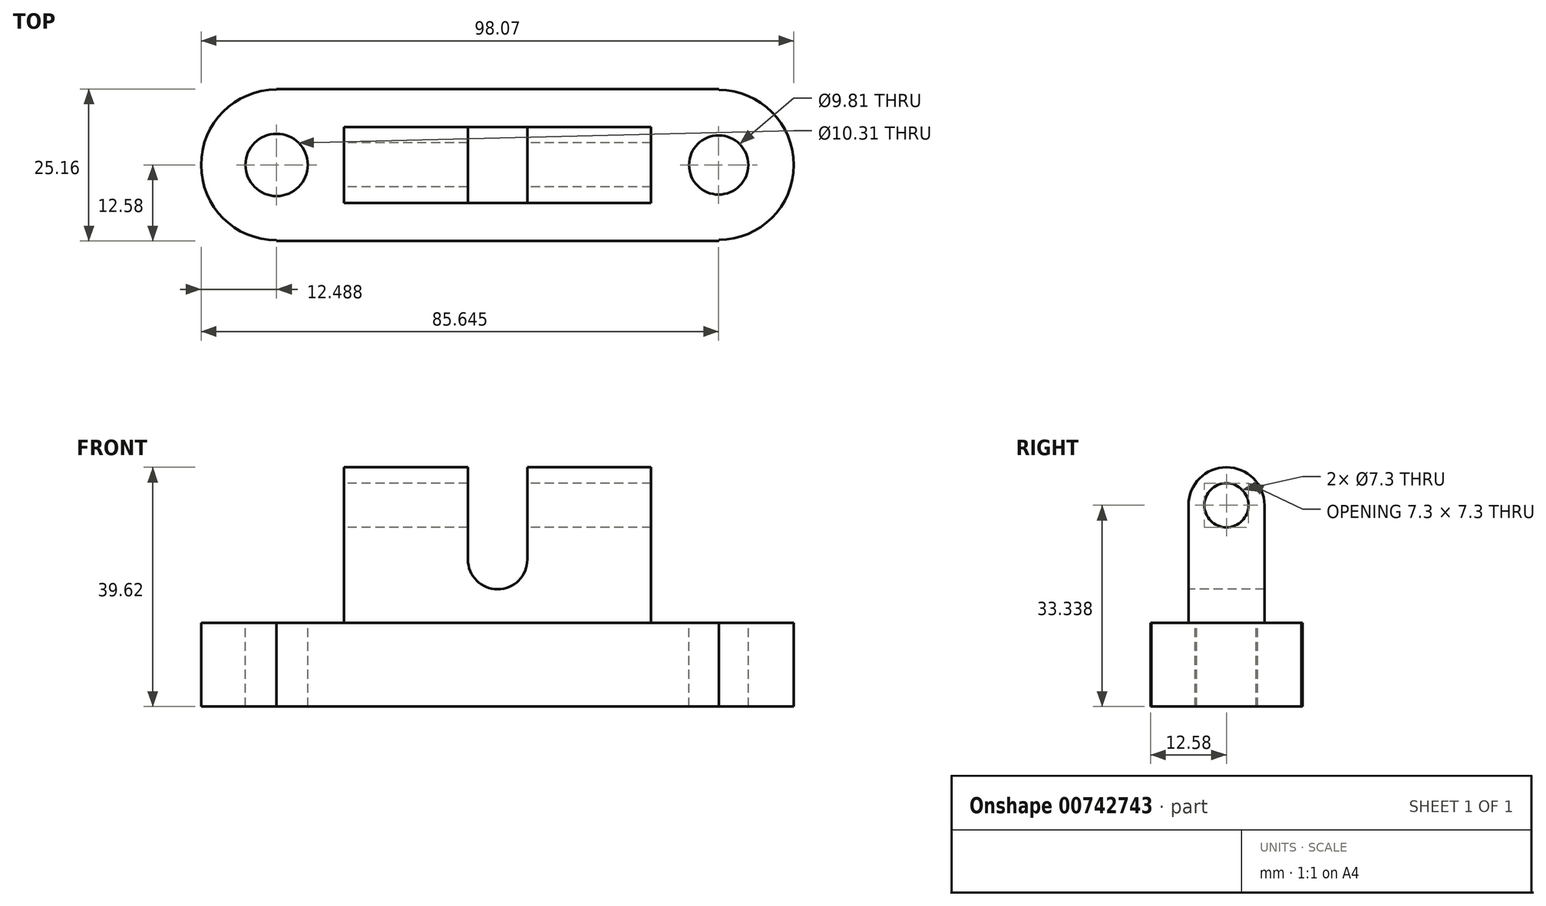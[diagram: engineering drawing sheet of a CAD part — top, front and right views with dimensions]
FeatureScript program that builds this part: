
annotation { "Feature Type Name" : "Feature", "Feature Type Description" : "" }
export const myFeature = defineFeature(function(context is Context, id is Id, definition is map)
    precondition{}
    {
        {
            var Q0;
            Q0=qCreatedBy(makeId("Top.planeOp"),FACE);
            var sketch = newSketch(context, id + "F0", { "sketchPlane" : qUnion([Q0])});
            skLineSegment(sketch, "E0.bottom", {"start": v(36.6, 12.58) * mm, "end": v(-36.6, 12.58) * mm});
            skLineSegment(sketch, "E0.top", {"start": v(36.6, -12.58) * mm, "end": v(-36.6, -12.58) * mm});
            skLineSegment(sketch, "E0.left", {"start": v(36.6, 12.58) * mm, "end": v(36.6, 12.4) * mm});
            skLineSegment(sketch, "E0.right", {"start": v(-36.6, 12.58) * mm, "end": v(-36.6, 12.47) * mm});
            skPoint(sketch, "E0.middle", {"position": v(0, 0) * mm});
            skArc(sketch, "E1", {"start": v(36.6, -12.4) * mm, "mid": v(49, 0) * mm, "end": v(36.6, 12.4) * mm});
            skArc(sketch, "E2", {"start": v(-36.6, 12.47) * mm, "mid": v(-49.07, 0) * mm, "end": v(-36.6, -12.47) * mm});
            skLineSegment(sketch, "E3.trimOffspring", {"start": v(-36.6, -12.47) * mm, "end": v(-36.6, -12.58) * mm});
            skLineSegment(sketch, "E4.trimOffspring", {"start": v(36.6, -12.4) * mm, "end": v(36.6, -12.58) * mm});
            skSolve(sketch);
        }
        {
            var Q0;
            Q0=qCreatedBy(makeId("Top.planeOp"),FACE);
            var sketch = newSketch(context, id + "F1", { "sketchPlane" : qUnion([Q0])});
            skCircle(sketch, "E5", {"center": v(-36.58, 0) * mm, "radius": 5.16 * mm});
            skCircle(sketch, "E6", {"center": v(36.58, 0) * mm, "radius": 4.9 * mm});
            skSolve(sketch);
        }
        {
            var Q0;
            Q0=makeQuery(id+"F0.imprint","IMPRINT",FACE,{"disambiguationData":[TD([[makeQuery(id+"F0.imprint","IMPRINT",EDGE,{"derivedFrom":sQuery(id+"F0.wireOp",EDGE,"E0.bottom")}),1.0]])]});
            var Q1;
            Q1 = qSketchRegion(id + "F1", true);
            extrude(context, id + "F2", {"entities" : qUnion([Q0, Q1]), "depth" : 13.85 * mm, "offsetDistance" : 25.4 * mm});
        }
        {
            var Q0;
            Q0=makeQuery(id+"F2.opExtrude","CAP_FACE",FACE,{"disambiguationData":[OSD([sQuery(id+"F1.wireOp",EDGE,"E6")])],"isStart":false});
            extrude(context, id + "F3", {"entities" : qUnion([Q0]), "operationType" : NewBodyOperationType.REMOVE, "oppositeDirection" : true, "depth" : 19.65 * mm, "offsetDistance" : 25.4 * mm});
        }
        {
            var Q0;
            Q0=makeQuery(id+"F2.opExtrude","CAP_FACE",FACE,{"disambiguationData":[OSD([sQuery(id+"F1.wireOp",EDGE,"E5")])],"isStart":false});
            extrude(context, id + "F4", {"entities" : qUnion([Q0]), "operationType" : NewBodyOperationType.REMOVE, "oppositeDirection" : true, "depth" : 33.9 * mm, "offsetDistance" : 25.4 * mm});
        }
        {
            var Q0;
            Q0=qCreatedBy(makeId("Right.planeOp"),FACE);
            var sketch = newSketch(context, id + "F5", { "sketchPlane" : qUnion([Q0])});
            skLineSegment(sketch, "E7.bottom", {"start": v(6.29, 33.34) * mm, "end": v(3.65, 33.34) * mm});
            skLineSegment(sketch, "E7.top", {"start": v(6.29, 4.74) * mm, "end": v(-6.29, 4.74) * mm});
            skLineSegment(sketch, "E7.left", {"start": v(6.29, 33.34) * mm, "end": v(6.29, 4.74) * mm});
            skLineSegment(sketch, "E7.right", {"start": v(-6.29, 33.34) * mm, "end": v(-6.29, 4.74) * mm});
            skPoint(sketch, "E7.middle", {"position": v(0, 19.04) * mm});
            skCircle(sketch, "E8", {"center": v(0, 33.34) * mm, "radius": 6.29 * mm});
            skCircle(sketch, "E9", {"center": v(0, 33.34) * mm, "radius": 3.65 * mm});
            skLineSegment(sketch, "E10.trimOffspring", {"start": v(-3.65, 33.34) * mm, "end": v(-6.29, 33.34) * mm});
            skSolve(sketch);
        }
        {
            var Q0;
            Q0 = qSketchRegion(id + "F5", true);
            extrude(context, id + "F6", {"entities" : qUnion([Q0]), "operationType" : NewBodyOperationType.ADD, "depth" : 25.4 * mm, "offsetDistance" : 25.4 * mm, "hasSecondDirection" : true, "secondDirectionOppositeDirection" : true, "secondDirectionDepth" : 25.4 * mm});
        }
        {
            var Q0;
            Q0=qCreatedBy(makeId("Front.planeOp"),FACE);
            var sketch = newSketch(context, id + "F7", { "sketchPlane" : qUnion([Q0])});
            skLineSegment(sketch, "E11.bottom", {"start": v(4.92, 50.46) * mm, "end": v(-4.92, 50.46) * mm});
            skLineSegment(sketch, "E11.top", {"start": v(4.92, 24.36) * mm, "end": v(-4.92, 24.36) * mm});
            skLineSegment(sketch, "E11.left", {"start": v(4.92, 50.46) * mm, "end": v(4.92, 24.36) * mm});
            skLineSegment(sketch, "E11.right", {"start": v(-4.92, 50.46) * mm, "end": v(-4.92, 24.36) * mm});
            skPoint(sketch, "E11.middle", {"position": v(0, 37.4) * mm});
            skCircle(sketch, "E12", {"center": v(0, 24.36) * mm, "radius": 4.92 * mm});
            skSolve(sketch);
        }
        {
            var Q0;
            Q0 = qSketchRegion(id + "F7", true);
            extrude(context, id + "F8", {"entities" : qUnion([Q0]), "operationType" : NewBodyOperationType.REMOVE, "oppositeDirection" : true, "depth" : 25.4 * mm, "offsetDistance" : 25.4 * mm, "hasSecondDirection" : true, "secondDirectionOppositeDirection" : false, "secondDirectionDepth" : 25.4 * mm});
        }
    });
